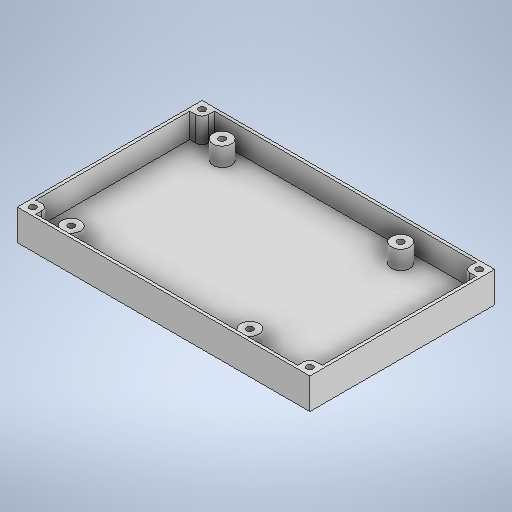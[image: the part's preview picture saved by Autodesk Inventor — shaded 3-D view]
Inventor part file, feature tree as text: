
AUTODESK INVENTOR PART (.ipt)
format: ipt  version: 2025 (Build 290162000, 162)  size: 339,968 bytes
history: native  units: mm
features: sketch x11, extrude x6, hole x5, other x1, fillet x1
ambient origin geometry x8: Origin, YZ Plane, XZ Plane, XY Plane, X Axis, Y Axis, Z Axis, Center Point
bodies: Body1 (feature_tree)
feature tree (24):
  other  "Bryła1"
  extrude  "Wyciągnięcie proste1"  Depth=90.0mm
  extrude  "Wyciągnięcie proste4"  Depth=60.0mm
  hole  "Otwór1"  [1 undecoded]
  hole  "Otwór2"  [1 undecoded]
  hole  "Otwór3"  [1 undecoded]
  hole  "Otwór4"  [1 undecoded]
  extrude  "Wyciągnięcie proste5"  Depth=6.0mm
  extrude  "Wyciągnięcie proste6"  Depth=6.0mm
  extrude  "Wyciągnięcie proste8"  TaperAngle=0.0deg  [1 undecoded]
  extrude  "Wyciągnięcie proste9"  Depth=5.0mm TaperAngle=0.0deg
  fillet  "Zaokrąglenie1"  Radius=8.0mm
  hole  "Otwór5"  [1 undecoded]
  sketch  "Szkic1"
  sketch  "Szkic10"
  sketch  "Szkic11"
  sketch  "Szkic12"
  sketch  "Szkic13"
  sketch  "Szkic14"
  sketch  "Szkic15"
  sketch  "Szkic16"
  sketch  "Szkic21"
  sketch  "Szkic22"
  sketch  "Szkic23"
note: 6 required parameter values undecoded (feature->parameter linkage not recoverable at this tier; creation-order binding heuristic only, values carry confidence <= 0.55)
